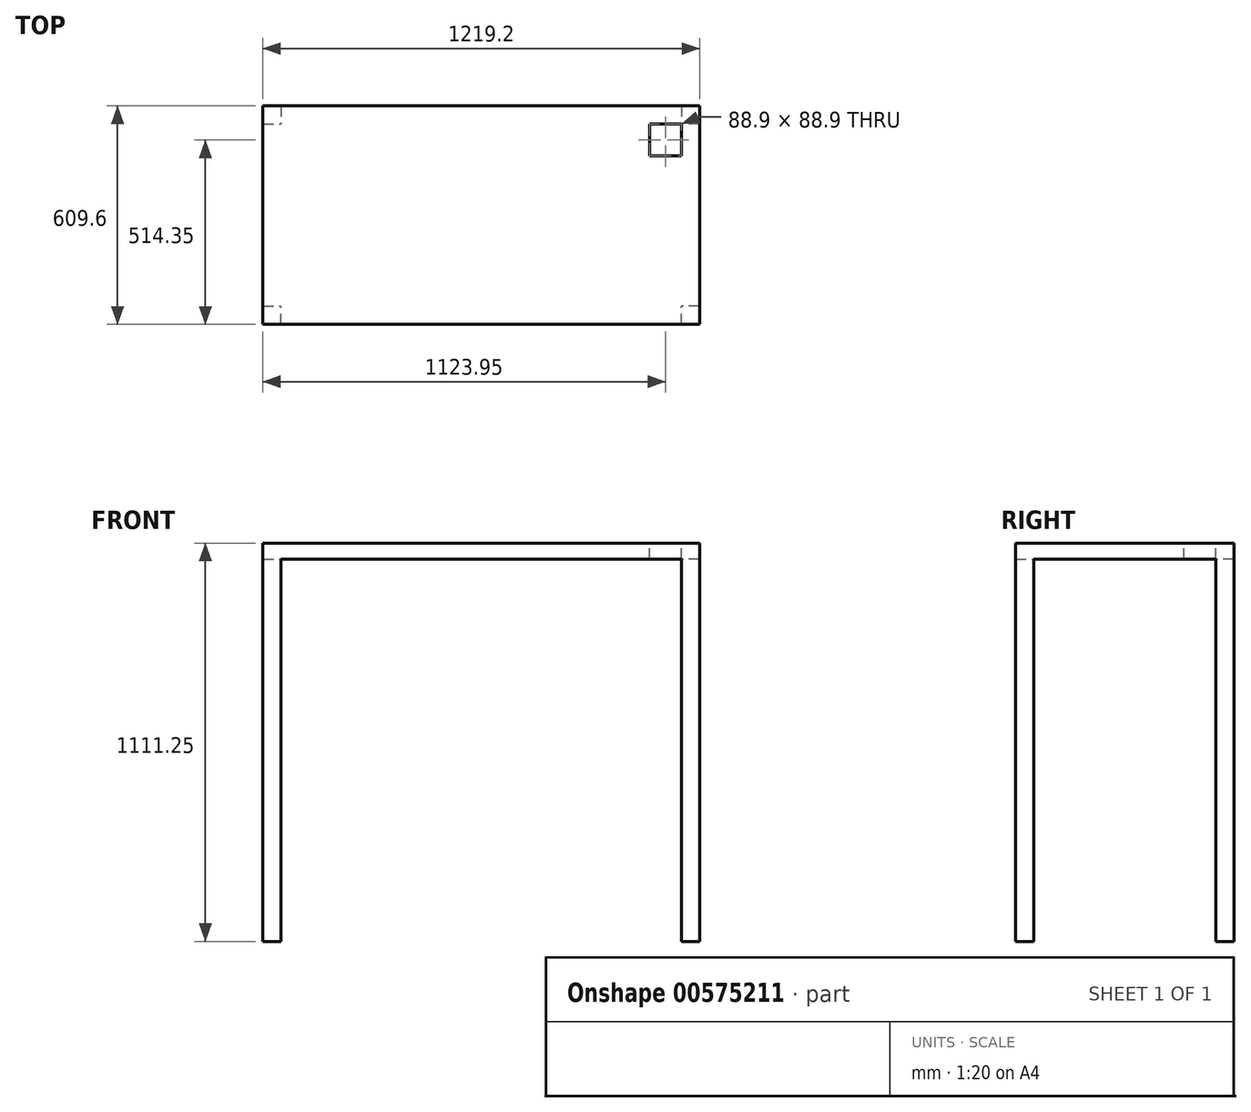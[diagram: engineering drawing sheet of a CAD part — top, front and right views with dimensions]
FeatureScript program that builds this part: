
annotation { "Feature Type Name" : "Feature", "Feature Type Description" : "" }
export const myFeature = defineFeature(function(context is Context, id is Id, definition is map)
    precondition{}
    {
        {
            var Q0;
            Q0=qCreatedBy(makeId("Top.planeOp"),FACE);
            var sketch = newSketch(context, id + "F0", { "sketchPlane" : qUnion([Q0])});
            skLineSegment(sketch, "E0.bottom", {"start": v(609.6, 304.8) * mm, "end": v(-609.6, 304.8) * mm});
            skLineSegment(sketch, "E0.top", {"start": v(609.6, -304.8) * mm, "end": v(-609.6, -304.8) * mm});
            skLineSegment(sketch, "E0.left", {"start": v(609.6, 304.8) * mm, "end": v(609.6, -304.8) * mm});
            skLineSegment(sketch, "E0.right", {"start": v(-609.6, 304.8) * mm, "end": v(-609.6, -304.8) * mm});
            skPoint(sketch, "E0.middle", {"position": v(0, 0) * mm});
            skSolve(sketch);
        }
        {
            var Q0;
            Q0 = qSketchRegion(id + "F0", true);
            extrude(context, id + "F1", {"entities" : qUnion([Q0]), "depth" : 44.45 * mm, "offsetDistance" : 25.4 * mm});
        }
        {
            var Q0;
            Q0=makeQuery(id+"F1.opExtrude","CAP_FACE",FACE,{"disambiguationData":[OSD([sQuery(id+"F0.wireOp",EDGE,"E0.bottom"),sQuery(id+"F0.wireOp",EDGE,"E0.top"),sQuery(id+"F0.wireOp",EDGE,"E0.left"),sQuery(id+"F0.wireOp",EDGE,"E0.right")])],"isStart":false});
            var sketch = newSketch(context, id + "F2", { "sketchPlane" : qUnion([Q0])});
            skLineSegment(sketch, "E1.bottom", {"start": v(558.8, 254) * mm, "end": v(469.9, 254) * mm});
            skLineSegment(sketch, "E1.top", {"start": v(558.8, 165.1) * mm, "end": v(469.9, 165.1) * mm});
            skLineSegment(sketch, "E1.left", {"start": v(558.8, 254) * mm, "end": v(558.8, 165.1) * mm});
            skLineSegment(sketch, "E1.right", {"start": v(469.9, 254) * mm, "end": v(469.9, 165.1) * mm});
            skPoint(sketch, "E1.middle", {"position": v(514.35, 209.55) * mm});
            skSolve(sketch);
        }
        {
            var Q0;
            Q0 = qSketchRegion(id + "F2", true);
            extrude(context, id + "F3", {"entities" : qUnion([Q0]), "operationType" : NewBodyOperationType.REMOVE, "endBound" : BoundingType.THROUGH_ALL, "oppositeDirection" : true, "depth" : 25.4 * mm, "offsetDistance" : 25.4 * mm});
        }
        {
            var Q0;
            Q0=makeQuery(id+"F1.opExtrude","CAP_FACE",FACE,{"disambiguationData":[OSD([sQuery(id+"F0.wireOp",EDGE,"E0.bottom"),sQuery(id+"F0.wireOp",EDGE,"E0.top"),sQuery(id+"F0.wireOp",EDGE,"E0.left"),sQuery(id+"F0.wireOp",EDGE,"E0.right")])],"isStart":true});
            var sketch = newSketch(context, id + "F4", { "sketchPlane" : qUnion([Q0])});
            skLineSegment(sketch, "E2.bottom", {"start": v(609.6, 304.8) * mm, "end": v(558.8, 304.8) * mm});
            skLineSegment(sketch, "E2.top", {"start": v(609.6, 254) * mm, "end": v(558.8, 254) * mm});
            skLineSegment(sketch, "E2.left", {"start": v(609.6, 304.8) * mm, "end": v(609.6, 254) * mm});
            skLineSegment(sketch, "E2.right", {"start": v(558.8, 304.8) * mm, "end": v(558.8, 254) * mm});
            skLineSegment(sketch, "E3.MirrorCS", {"start": v(-558.8, 304.8) * mm, "end": v(-558.8, 254) * mm});
            skLineSegment(sketch, "E4.MirrorCS", {"start": v(-609.6, 304.8) * mm, "end": v(-558.8, 304.8) * mm});
            skLineSegment(sketch, "E5.MirrorCS", {"start": v(-609.6, 254) * mm, "end": v(-558.8, 254) * mm});
            skLineSegment(sketch, "E6.MirrorCS", {"start": v(-609.6, 304.8) * mm, "end": v(-609.6, 254) * mm});
            skLineSegment(sketch, "E7.MirrorCS", {"start": v(-609.6, -254) * mm, "end": v(-558.8, -254) * mm});
            skLineSegment(sketch, "E8.MirrorCS", {"start": v(-609.6, -304.8) * mm, "end": v(-558.8, -304.8) * mm});
            skLineSegment(sketch, "E9.MirrorCS", {"start": v(-558.8, -304.8) * mm, "end": v(-558.8, -254) * mm});
            skLineSegment(sketch, "E10.MirrorCS", {"start": v(-609.6, -304.8) * mm, "end": v(-609.6, -254) * mm});
            skLineSegment(sketch, "E11.MirrorCS", {"start": v(558.8, -304.8) * mm, "end": v(558.8, -254) * mm});
            skLineSegment(sketch, "E12.MirrorCS", {"start": v(609.6, -304.8) * mm, "end": v(558.8, -304.8) * mm});
            skLineSegment(sketch, "E13.MirrorCS", {"start": v(609.6, -304.8) * mm, "end": v(609.6, -254) * mm});
            skLineSegment(sketch, "E14.MirrorCS", {"start": v(609.6, -254) * mm, "end": v(558.8, -254) * mm});
            skSolve(sketch);
        }
        {
            var Q0;
            Q0 = qSketchRegion(id + "F4", true);
            extrude(context, id + "F5", {"entities" : qUnion([Q0]), "operationType" : NewBodyOperationType.ADD, "depth" : 1066.8 * mm, "offsetDistance" : 25.4 * mm});
        }
    });
